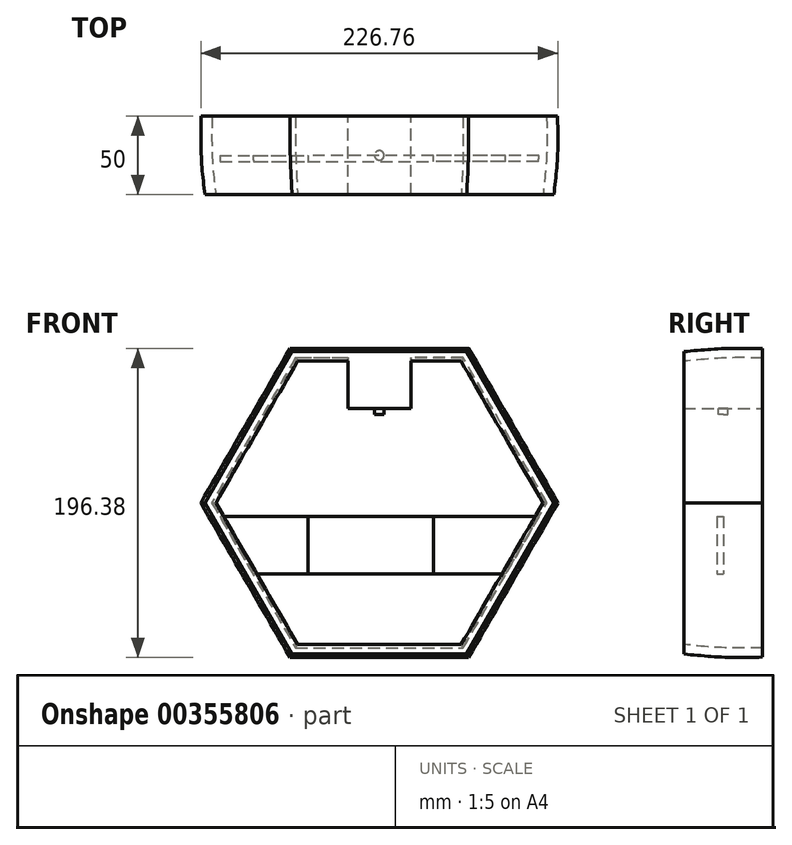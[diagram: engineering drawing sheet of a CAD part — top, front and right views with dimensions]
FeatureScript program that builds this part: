
annotation { "Feature Type Name" : "Feature", "Feature Type Description" : "" }
export const myFeature = defineFeature(function(context is Context, id is Id, definition is map)
    precondition{}
    {
        {
            var Q0;
            Q0=qCreatedBy(makeId("Front.planeOp"),FACE);
            var sketch = newSketch(context, id + "F0", { "sketchPlane" : qUnion([Q0])});
            skCircle(sketch, "E0.cCircle", {"center": v(0, 0) * mm, "radius": 98 * mm, "construction": true});
            skLineSegment(sketch, "E0.0", {"start": v(-56.58, 98) * mm, "end": v(56.58, 98) * mm});
            skLineSegment(sketch, "E0.1", {"start": v(56.58, 98) * mm, "end": v(113.16, 0) * mm});
            skLineSegment(sketch, "E0.2", {"start": v(113.16, 0) * mm, "end": v(56.58, -98) * mm});
            skLineSegment(sketch, "E0.3", {"start": v(56.58, -98) * mm, "end": v(-56.58, -98) * mm});
            skLineSegment(sketch, "E0.4", {"start": v(-56.58, -98) * mm, "end": v(-113.16, 0) * mm});
            skLineSegment(sketch, "E0.5", {"start": v(-113.16, 0) * mm, "end": v(-56.58, 98) * mm});
            skPoint(sketch, "E0.0.midPoint", {"position": v(0, 98) * mm});
            skSolve(sketch);
        }
        {
            var Q0;
            Q0=qCreatedBy(makeId("Front.planeOp"),FACE);
            cPlane(context, id + "F1", {"entities" : qUnion([Q0]), "cplaneType" : CPlaneType.OFFSET, "offset" : 25 * mm, "oppositeDirection" : true, "width" : 150 * mm, "height" : 150 * mm});
        }
        {
            var Q0;
            Q0=qCreatedBy(id+"F1.planeOp",FACE);
            var sketch = newSketch(context, id + "F2", { "sketchPlane" : qUnion([Q0])});
            skCircle(sketch, "E1.cCircle", {"center": v(0, 0) * mm, "radius": 98 * mm, "construction": true});
            skLineSegment(sketch, "E1.0", {"start": v(-56.58, 98) * mm, "end": v(56.58, 98) * mm});
            skLineSegment(sketch, "E1.1", {"start": v(56.58, 98) * mm, "end": v(113.16, 0) * mm});
            skLineSegment(sketch, "E1.2", {"start": v(113.16, 0) * mm, "end": v(56.58, -98) * mm});
            skLineSegment(sketch, "E1.3", {"start": v(56.58, -98) * mm, "end": v(-56.58, -98) * mm});
            skLineSegment(sketch, "E1.4", {"start": v(-56.58, -98) * mm, "end": v(-113.16, 0) * mm});
            skLineSegment(sketch, "E1.5", {"start": v(-113.16, 0) * mm, "end": v(-56.58, 98) * mm});
            skPoint(sketch, "E1.0.midPoint", {"position": v(0, 98) * mm});
            skSolve(sketch);
        }
        {
            var Q0;
            Q0=qCreatedBy(makeId("Front.planeOp"),FACE);
            cPlane(context, id + "F3", {"entities" : qUnion([Q0]), "cplaneType" : CPlaneType.OFFSET, "offset" : 25 * mm, "width" : 150 * mm, "height" : 150 * mm});
        }
        {
            var Q0;
            Q0=qCreatedBy(id+"F3.planeOp",FACE);
            var sketch = newSketch(context, id + "F4", { "sketchPlane" : qUnion([Q0])});
            skCircle(sketch, "E2.cCircle", {"center": v(0, 0) * mm, "radius": 96 * mm, "construction": true});
            skLineSegment(sketch, "E2.0", {"start": v(55.43, -96) * mm, "end": v(-55.43, -96) * mm});
            skLineSegment(sketch, "E2.1", {"start": v(-55.43, -96) * mm, "end": v(-110.85, 0) * mm});
            skLineSegment(sketch, "E2.2", {"start": v(-110.85, 0) * mm, "end": v(-55.43, 96) * mm});
            skLineSegment(sketch, "E2.3", {"start": v(-55.43, 96) * mm, "end": v(55.43, 96) * mm});
            skLineSegment(sketch, "E2.4", {"start": v(55.43, 96) * mm, "end": v(110.85, 0) * mm});
            skLineSegment(sketch, "E2.5", {"start": v(110.85, 0) * mm, "end": v(55.43, -96) * mm});
            skPoint(sketch, "E2.0.midPoint", {"position": v(0, -96) * mm});
            skSolve(sketch);
        }
        {
            var Q0;
            Q0=makeQuery(id+"F2.imprint","IMPRINT",FACE,{"disambiguationData":[TD([[makeQuery(id+"F2.imprint","IMPRINT",EDGE,{"derivedFrom":sQuery(id+"F2.wireOp",EDGE,"E1.0")}),-1.0]])]});
            var Q1;
            Q1=makeQuery(id+"F0.imprint","IMPRINT",FACE,{"disambiguationData":[TD([[makeQuery(id+"F0.imprint","IMPRINT",EDGE,{"derivedFrom":sQuery(id+"F0.wireOp",EDGE,"E0.0")}),-1.0]])]});
            var Q2;
            Q2=makeQuery(id+"F4.imprint","IMPRINT",FACE,{"disambiguationData":[TD([[makeQuery(id+"F4.imprint","IMPRINT",EDGE,{"derivedFrom":sQuery(id+"F4.wireOp",EDGE,"E2.0")}),-1.0]])]});
            loft(context, id + "F5", {"sheetProfilesArray" : [{ "sheetProfileEntities" : qUnion([Q0]) }, { "sheetProfileEntities" : qUnion([Q1]) }, { "sheetProfileEntities" : qUnion([Q2]) }]});
        }
        {
            var Q0;
            Q0=makeQuery(id+"F5.opLoft","CAP_FACE",FACE,{"disambiguationData":[OSD([makeQuery(id+"F2.imprint","IMPRINT",FACE,{"disambiguationData":[TD([[makeQuery(id+"F2.imprint","IMPRINT",EDGE,{"derivedFrom":sQuery(id+"F2.wireOp",EDGE,"E1.0")}),-1.0]])]})])],"isStart":true});
            var Q1;
            Q1=makeQuery(id+"F5.opLoft","CAP_FACE",FACE,{"disambiguationData":[OSD([makeQuery(id+"F4.imprint","IMPRINT",FACE,{"disambiguationData":[TD([[makeQuery(id+"F4.imprint","IMPRINT",EDGE,{"derivedFrom":sQuery(id+"F4.wireOp",EDGE,"E2.0")}),-1.0]])]})])],"isStart":true});
            shell(context, id + "F6", {"entities" : qUnion([Q0, Q1]), "thickness" : 6 * mm});
        }
        {
            var Q0;
            Q0=qCreatedBy(makeId("Top.planeOp"),FACE);
            cPlane(context, id + "F7", {"entities" : qUnion([Q0]), "cplaneType" : CPlaneType.OFFSET, "offset" : 45 * mm, "oppositeDirection" : true, "width" : 150 * mm, "height" : 150 * mm});
        }
        {
            var Q0;
            Q0=qCreatedBy(id+"F7.planeOp",FACE);
            var sketch = newSketch(context, id + "F8", { "sketchPlane" : qUnion([Q0])});
            skLineSegment(sketch, "E3", {"start": v(34.28, 0) * mm, "end": v(-45.28, 0) * mm});
            skLineSegment(sketch, "E4", {"start": v(-45.28, 0) * mm, "end": v(-45.28, -4) * mm});
            skLineSegment(sketch, "E5", {"start": v(-45.28, -4) * mm, "end": v(34.28, -4) * mm});
            skLineSegment(sketch, "E6", {"start": v(34.28, -4) * mm, "end": v(34.28, 0) * mm});
            skSolve(sketch);
        }
        {
            var Q0;
            Q0=qSketchRegion(id+"F8",true);
            extrude(context, id + "F9", {"entities" : qUnion([Q0]), "depth" : 36.5 * mm});
        }
        {
            var Q0;
            Q0=makeQuery(id+"F9.opExtrude","SWEPT_FACE",FACE,{"disambiguationData":[OSD([sQuery(id+"F8.wireOp",EDGE,"E4")])]});
            extrude(context, id + "F10", {"entities" : qUnion([Q0]), "endBound" : BoundingType.UP_TO_NEXT, "depth" : 25 * mm});
        }
        {
            var Q0;
            Q0=makeQuery(id+"F9.opExtrude","SWEPT_FACE",FACE,{"disambiguationData":[OSD([sQuery(id+"F8.wireOp",EDGE,"E6")])]});
            extrude(context, id + "F11", {"entities" : qUnion([Q0]), "endBound" : BoundingType.UP_TO_NEXT, "depth" : 25 * mm});
        }
        {
            var Q0;
            Q0=qCreatedBy(makeId("Top.planeOp"),FACE);
            cPlane(context, id + "F12", {"entities" : qUnion([Q0]), "cplaneType" : CPlaneType.OFFSET, "offset" : 60 * mm, "width" : 150 * mm, "height" : 150 * mm});
        }
        {
            var Q0;
            Q0=qCreatedBy(id+"F12.planeOp",FACE);
            var sketch = newSketch(context, id + "F13", { "sketchPlane" : qUnion([Q0])});
            skLineSegment(sketch, "E7.0", {"start": v(20, -25) * mm, "end": v(-20, -25) * mm});
            skLineSegment(sketch, "E8.0", {"start": v(20, 25) * mm, "end": v(-20, 25) * mm});
            skLineSegment(sketch, "E9", {"start": v(-20, -25) * mm, "end": v(-20, 25) * mm});
            skLineSegment(sketch, "E10", {"start": v(20, -25) * mm, "end": v(20, 25) * mm});
            skPoint(sketch, "E11.orphan", {"position": v(-56.58, 25) * mm});
            skPoint(sketch, "E12.orphan", {"position": v(-55.43, -25) * mm});
            skPoint(sketch, "E13.orphan", {"position": v(55.43, -25) * mm});
            skPoint(sketch, "E14.orphan", {"position": v(56.58, 25) * mm});
            skSolve(sketch);
        }
        {
            var Q0;
            Q0=qSketchRegion(id+"F13",true);
            extrude(context, id + "F14", {"entities" : qUnion([Q0]), "operationType" : NewBodyOperationType.ADD, "endBound" : BoundingType.UP_TO_NEXT, "depth" : 25 * mm});
        }
        {
            var Q0;
            Q0=makeQuery(id+"F14.opExtrude","CAP_FACE",FACE,{"disambiguationData":[OSD([sQuery(id+"F13.wireOp",EDGE,"E7.0"),sQuery(id+"F13.wireOp",EDGE,"E8.0"),sQuery(id+"F13.wireOp",EDGE,"E9"),sQuery(id+"F13.wireOp",EDGE,"E10")])],"isStart":true});
            var sketch = newSketch(context, id + "F15", { "sketchPlane" : qUnion([Q0])});
            skCircle(sketch, "E15", {"center": v(0, 0) * mm, "radius": 3 * mm});
            skSolve(sketch);
        }
        {
            var Q0;
            Q0=qSketchRegion(id+"F15",true);
            extrude(context, id + "F16", {"entities" : qUnion([Q0]), "operationType" : NewBodyOperationType.ADD, "depth" : 4 * mm});
        }
    });
